# Revit family: Lighting-Wall-Cooper-Ametrix-Asyx-2-WM-LED
name_source: partatom
category: Lighting Fixtures
revit_build: Autodesk Revit 2014 (Build: 20130308_1515(x64)
units: mm (PartAtom-declared; Revit-internal decimal feet)

## types (1)
- Lighting-Wall-Cooper-Ametrix-Asyx-2-WM-LED
    0 Degrees = Yes
    120 Volt = Yes
    20 Degrees Down = No
    20 Degrees Up = No
    Apparent Load = 0 VA
    Assembly Code = D5020200
    Color Filter = 16777215
    Connector Description = Power In
    Default Elevation = 0' - 0"
    Description = Asymmetric LED Direct & Indirect
    Dimming Lamp Color Temperature Shift = <None>
    Finish = Finish - Cooper Industries - White
    Fins Array = 27
    Fins Width = 1' - 4 3/4"
    Fixture Angle = 0
    Frequency = 50 Hz
    Housing Depth = 0' - 2 1/2"
    Housing Height = 1' - 7 3/16"
    Housing Width = 1' - 6"
    Lamp = LED
    Load Classification = Lighting
    Manufacturer = Cooper Lighting
    Model = WM
    Mounting = Wall
    Mounting Plate Height = 0' - 6"
    Mounting Plate Width = 0' - 6"
    Number of LightBARs = 3
    Photometric Web File = ASYX-S-L-F-X-X-L27-1-STD-UNV.ies
    Power (Wattage) = 70 W
    Power Factor = 0.9
    Product Page URL = http://www.cooperindustries.com
    Tilt Angle = 90.00°
    Type Comments = Wall Mount
    URL = www.eaton.com/lighting
    Voltage = 120 V

## geometry (parser evidence)
native form markers: Blend x4, Sweep x5
no freeform markers — native parametric forms only
